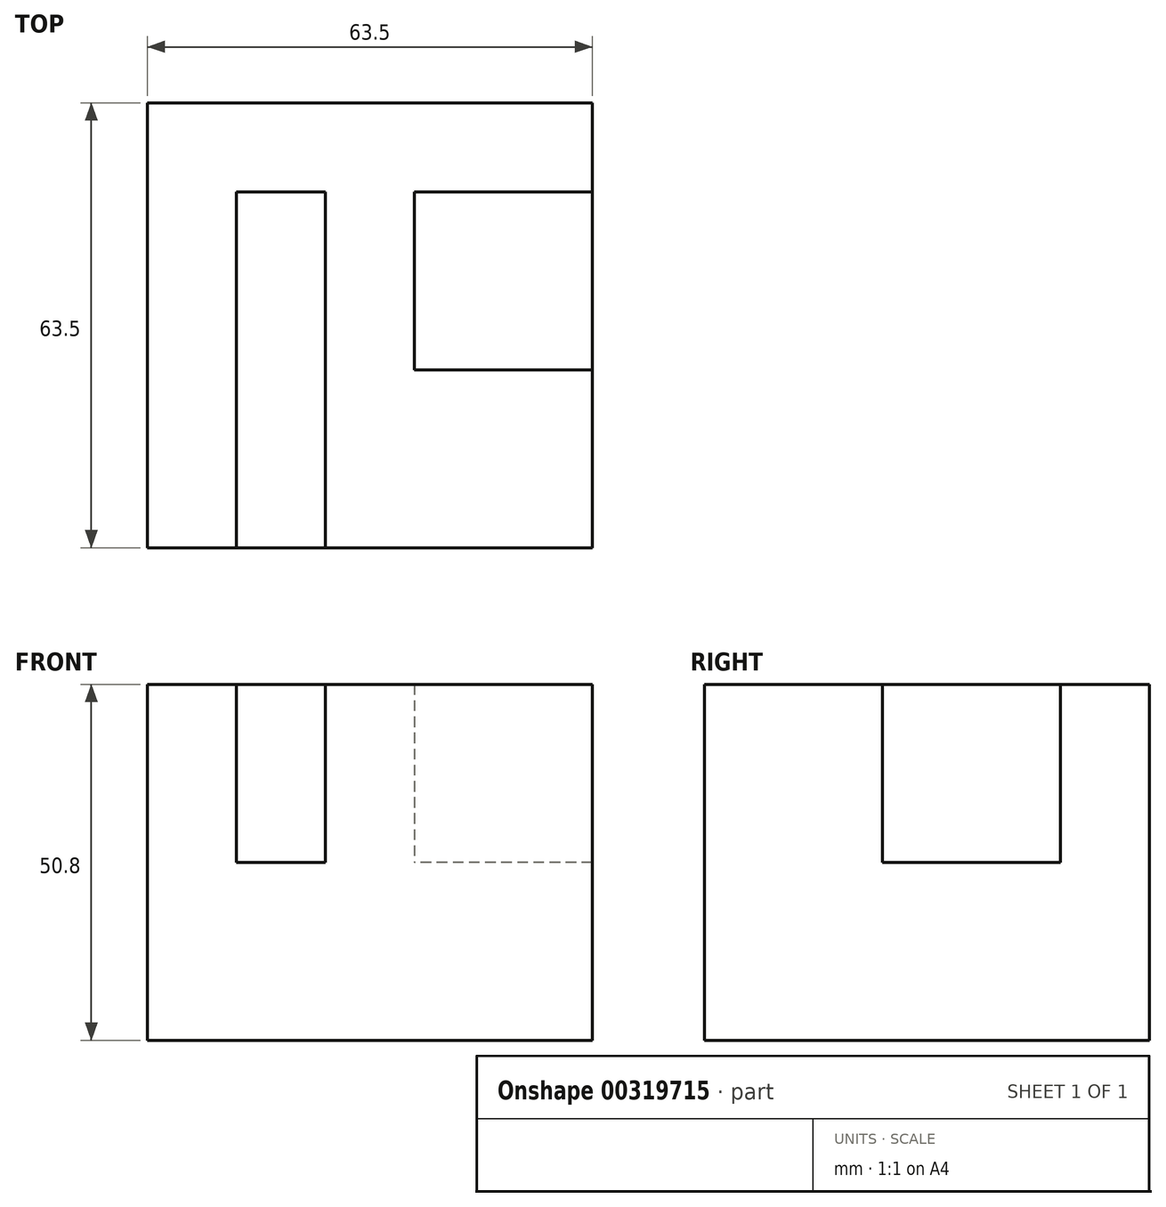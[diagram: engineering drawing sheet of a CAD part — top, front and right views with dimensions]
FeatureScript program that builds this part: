
annotation { "Feature Type Name" : "Feature", "Feature Type Description" : "" }
export const myFeature = defineFeature(function(context is Context, id is Id, definition is map)
    precondition{}
    {
        {
            var Q0;
            Q0=qCreatedBy(makeId("Front.planeOp"),FACE);
            var sketch = newSketch(context, id + "F0", { "sketchPlane" : qUnion([Q0])});
            skLineSegment(sketch, "E0.bottom", {"start": v(-31.75, 25.4) * mm, "end": v(6.35, 25.4) * mm});
            skLineSegment(sketch, "E0.top", {"start": v(-31.75, -25.4) * mm, "end": v(6.35, -25.4) * mm});
            skLineSegment(sketch, "E0.left", {"start": v(-31.75, 25.4) * mm, "end": v(-31.75, -25.4) * mm});
            skLineSegment(sketch, "E0.right", {"start": v(6.35, 25.4) * mm, "end": v(6.35, -25.4) * mm});
            skLineSegment(sketch, "E1.bottom", {"start": v(-19.05, 25.4) * mm, "end": v(-6.35, 25.4) * mm});
            skLineSegment(sketch, "E1.top", {"start": v(-19.05, 0) * mm, "end": v(-6.35, 0) * mm});
            skLineSegment(sketch, "E1.left", {"start": v(-19.05, 25.4) * mm, "end": v(-19.05, 0) * mm});
            skLineSegment(sketch, "E1.right", {"start": v(-6.35, 25.4) * mm, "end": v(-6.35, 0) * mm});
            skSolve(sketch);
        }
        {
            var Q0;
            Q0 = qSketchRegion(id + "F0", true);
            extrude(context, id + "F1", {"entities" : qUnion([Q0]), "depth" : 12.7 * mm});
        }
        {
            var Q0;
            Q0=makeQuery(id+"F0.imprint","IMPRINT",FACE,{"disambiguationData":[TD([[makeQuery(id+"F0.imprint","IMPRINT",EDGE,{"derivedFrom":sQuery(id+"F0.wireOp",EDGE,"E0.top")}),1.0]])]});
            extrude(context, id + "F2", {"entities" : qUnion([Q0]), "operationType" : NewBodyOperationType.ADD, "depth" : 63.5 * mm});
        }
        {
            var Q0;
            {var subQ0=sQuery(id+"F0.wireOp",EDGE,"E0.right");Q0=makeQuery(id+"F2.boolean.opBoolean","MERGE",FACE,{"derivedFrom":[makeQuery(id+"F1.opExtrude","SWEPT_FACE",FACE,{"disambiguationData":[OSD([subQ0])]}),makeQuery(id+"F2.opExtrude","SWEPT_FACE",FACE,{"disambiguationData":[OSD([subQ0])]})]});}
            var sketch = newSketch(context, id + "F3", { "sketchPlane" : qUnion([Q0])});
            skLineSegment(sketch, "E2.bottom", {"start": v(-38.1, 25.4) * mm, "end": v(-12.7, 25.4) * mm});
            skLineSegment(sketch, "E2.top", {"start": v(-38.1, 0) * mm, "end": v(-12.7, 0) * mm});
            skLineSegment(sketch, "E2.left", {"start": v(-38.1, 25.4) * mm, "end": v(-38.1, 0) * mm});
            skLineSegment(sketch, "E2.right", {"start": v(-12.7, 25.4) * mm, "end": v(-12.7, 0) * mm});
            skLineSegment(sketch, "E3.bottom", {"start": v(-63.5, 25.4) * mm, "end": v(0, 25.4) * mm});
            skLineSegment(sketch, "E3.top", {"start": v(-63.5, -25.4) * mm, "end": v(0, -25.4) * mm});
            skLineSegment(sketch, "E3.left", {"start": v(-63.5, 25.4) * mm, "end": v(-63.5, -25.4) * mm});
            skLineSegment(sketch, "E3.right", {"start": v(0, 25.4) * mm, "end": v(0, -25.4) * mm});
            skSolve(sketch);
        }
        {
            var Q0;
            Q0=makeQuery(id+"F3.imprint","IMPRINT",FACE,{"disambiguationData":[TD([[makeQuery(id+"F3.imprint","IMPRINT",EDGE,{"derivedFrom":sQuery(id+"F3.wireOp",EDGE,"E2.top")}),-1.0]])]});
            extrude(context, id + "F4", {"entities" : qUnion([Q0]), "operationType" : NewBodyOperationType.ADD, "depth" : 25.4 * mm});
        }
    });
